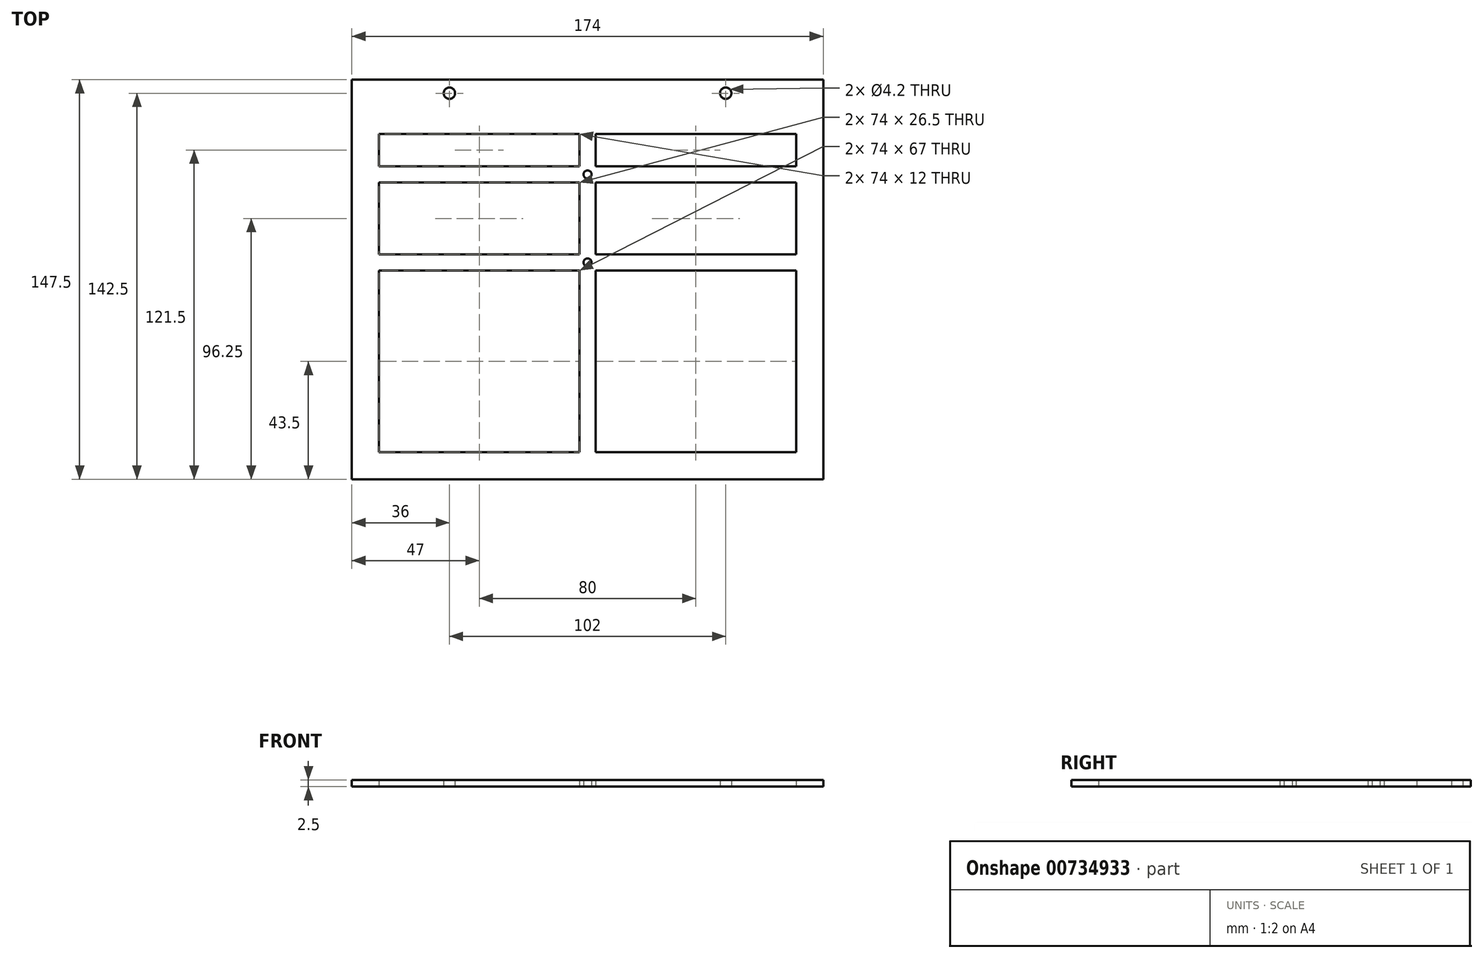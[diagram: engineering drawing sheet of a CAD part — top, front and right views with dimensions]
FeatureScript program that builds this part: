
annotation { "Feature Type Name" : "Feature", "Feature Type Description" : "" }
export const myFeature = defineFeature(function(context is Context, id is Id, definition is map)
    precondition{}
    {
        {
            var Q0;
            Q0=qCreatedBy(makeId("Top.planeOp"),FACE);
            var sketch = newSketch(context, id + "F0", { "sketchPlane" : qUnion([Q0])});
            skLineSegment(sketch, "E0.bottom", {"start": v(87, -80) * mm, "end": v(-87, -80) * mm});
            skLineSegment(sketch, "E0.top", {"start": v(87, 67.5) * mm, "end": v(-87, 67.5) * mm});
            skLineSegment(sketch, "E0.left", {"start": v(87, -80) * mm, "end": v(87, 67.5) * mm});
            skLineSegment(sketch, "E0.right", {"start": v(-87, -80) * mm, "end": v(-87, 67.5) * mm});
            skPoint(sketch, "E0.middle", {"position": v(0, 0) * mm});
            skCircle(sketch, "E1", {"center": v(-51, 62.5) * mm, "radius": 2.1 * mm});
            skCircle(sketch, "E2", {"center": v(51, 62.5) * mm, "radius": 2.1 * mm});
            skLineSegment(sketch, "E3.bottom", {"start": v(15, -23.5) * mm, "end": v(-15, -23.5) * mm, "construction": true});
            skLineSegment(sketch, "E3.top", {"start": v(15, 46.5) * mm, "end": v(-15, 46.5) * mm, "construction": true});
            skLineSegment(sketch, "E3.left", {"start": v(15, -23.5) * mm, "end": v(15, 46.5) * mm, "construction": true});
            skLineSegment(sketch, "E3.right", {"start": v(-15, -23.5) * mm, "end": v(-15, 46.5) * mm, "construction": true});
            skPoint(sketch, "E4", {"position": v(0, 46.5) * mm});
            skPoint(sketch, "E5", {"position": v(0, -23.5) * mm});
            skCircle(sketch, "E6", {"center": v(0, 32.5) * mm, "radius": 1.5 * mm});
            skCircle(sketch, "E7", {"center": v(0, 0) * mm, "radius": 1.5 * mm});
            skLineSegment(sketch, "E8", {"start": v(-87, 62.5) * mm, "end": v(87, 62.5) * mm, "construction": true});
            skLineSegment(sketch, "E9", {"start": v(-87, 57.5) * mm, "end": v(87, 57.5) * mm, "construction": true});
            skLineSegment(sketch, "E10.0", {"start": v(87, -70) * mm, "end": v(-87, -70) * mm, "construction": true});
            skLineSegment(sketch, "E11.0", {"start": v(-77, -80) * mm, "end": v(-77, 80) * mm, "construction": true});
            skLineSegment(sketch, "E12.0", {"start": v(77, -75) * mm, "end": v(77, 85) * mm, "construction": true});
            skLineSegment(sketch, "E13.0", {"start": v(-87, 47.5) * mm, "end": v(87, 47.5) * mm, "construction": true});
            skLineSegment(sketch, "E14.bottom", {"start": v(77, -70) * mm, "end": v(3, -70) * mm});
            skLineSegment(sketch, "E14.top", {"start": v(77, 47.5) * mm, "end": v(3, 47.5) * mm});
            skLineSegment(sketch, "E14.left", {"start": v(77, -70) * mm, "end": v(77, 47.5) * mm});
            skLineSegment(sketch, "E14.right", {"start": v(3, -70) * mm, "end": v(3, 47.5) * mm});
            skLineSegment(sketch, "E15.bottom", {"start": v(-77, -70) * mm, "end": v(-3, -70) * mm});
            skLineSegment(sketch, "E15.top", {"start": v(-77, 47.5) * mm, "end": v(-3, 47.5) * mm});
            skLineSegment(sketch, "E15.left", {"start": v(-77, -70) * mm, "end": v(-77, 47.5) * mm});
            skLineSegment(sketch, "E15.right", {"start": v(-3, -70) * mm, "end": v(-3, 47.5) * mm});
            skLineSegment(sketch, "E16.bottom", {"start": v(-77, 35.5) * mm, "end": v(77, 35.5) * mm});
            skLineSegment(sketch, "E16.top", {"start": v(-77, 29.5) * mm, "end": v(77, 29.5) * mm});
            skLineSegment(sketch, "E16.left", {"start": v(-77, 35.5) * mm, "end": v(-77, 29.5) * mm});
            skLineSegment(sketch, "E16.right", {"start": v(77, 35.5) * mm, "end": v(77, 29.5) * mm});
            skLineSegment(sketch, "E17.bottom", {"start": v(-77, 3) * mm, "end": v(77, 3) * mm});
            skLineSegment(sketch, "E17.top", {"start": v(-77, -3) * mm, "end": v(77, -3) * mm});
            skLineSegment(sketch, "E17.left", {"start": v(-77, 3) * mm, "end": v(-77, -3) * mm});
            skLineSegment(sketch, "E17.right", {"start": v(77, 3) * mm, "end": v(77, -3) * mm});
            skPoint(sketch, "E18", {"position": v(30.07, 0) * mm});
            skSolve(sketch);
        }
        {
            var Q0;
            Q0=makeQuery(id+"F0.imprint","IMPRINT",FACE,{"disambiguationData":[TD([[makeQuery(id+"F0.imprint","IMPRINT",EDGE,{"derivedFrom":sQuery(id+"F0.wireOp",EDGE,"E0.bottom")}),-1.0]])]});
            var Q1;
            Q1=makeQuery(id+"F0.imprint","IMPRINT",FACE,{"disambiguationData":[TD([[makeQuery(id+"F0.imprint","IMPRINT",EDGE,{"derivedFrom":sQuery(id+"F0.wireOp",EDGE,"E6")}),-1.0]])]});
            var Q2;
            {var subQ0=sQuery(id+"F0.wireOp",EDGE,"E16.top");var subQ1=sQuery(id+"F0.wireOp",EDGE,"E14.right");var subQ2=makeQuery(id+"F0.imprint","INTERSECT",VERTEX,{"derivedFrom":[subQ1,subQ0]});Q2=makeQuery(id+"F0.imprint","IMPRINT",FACE,{"disambiguationData":[TD([[makeQuery(id+"F0.imprint","IMPRINT",EDGE,{"disambiguationData":[TD([[subQ2,1.0]])],"derivedFrom":subQ1}),1.0]])]});}
            var Q3;
            Q3=makeQuery(id+"F0.imprint","IMPRINT",FACE,{"disambiguationData":[TD([[makeQuery(id+"F0.imprint","IMPRINT",EDGE,{"derivedFrom":sQuery(id+"F0.wireOp",EDGE,"E7")}),-1.0]])]});
            var Q4;
            {var subQ0=sQuery(id+"F0.wireOp",EDGE,"E17.top");var subQ1=sQuery(id+"F0.wireOp",EDGE,"E14.left");var subQ2=makeQuery(id+"F0.imprint","INTERSECT",VERTEX,{"derivedFrom":[subQ1,subQ0]});Q4=makeQuery(id+"F0.imprint","IMPRINT",FACE,{"disambiguationData":[TD([[makeQuery(id+"F0.imprint","IMPRINT",EDGE,{"disambiguationData":[TD([[subQ2,-1.0]])],"derivedFrom":subQ1}),1.0]])]});}
            var Q5;
            {var subQ0=sQuery(id+"F0.wireOp",EDGE,"E17.top");var subQ1=sQuery(id+"F0.wireOp",EDGE,"E15.left");var subQ2=makeQuery(id+"F0.imprint","INTERSECT",VERTEX,{"derivedFrom":[subQ1,subQ0]});Q5=makeQuery(id+"F0.imprint","IMPRINT",FACE,{"disambiguationData":[TD([[makeQuery(id+"F0.imprint","IMPRINT",EDGE,{"disambiguationData":[TD([[subQ2,-1.0]])],"derivedFrom":subQ1}),-1.0]])]});}
            var Q6;
            {var subQ0=sQuery(id+"F0.wireOp",EDGE,"E16.bottom");var subQ1=sQuery(id+"F0.wireOp",EDGE,"E15.left");var subQ2=makeQuery(id+"F0.imprint","INTERSECT",VERTEX,{"derivedFrom":[subQ1,subQ0]});Q6=makeQuery(id+"F0.imprint","IMPRINT",FACE,{"disambiguationData":[TD([[makeQuery(id+"F0.imprint","IMPRINT",EDGE,{"disambiguationData":[TD([[subQ2,1.0]])],"derivedFrom":subQ1}),-1.0]])]});}
            var Q7;
            {var subQ0=sQuery(id+"F0.wireOp",EDGE,"E16.bottom");var subQ1=sQuery(id+"F0.wireOp",EDGE,"E14.left");var subQ2=makeQuery(id+"F0.imprint","INTERSECT",VERTEX,{"derivedFrom":[subQ1,subQ0]});Q7=makeQuery(id+"F0.imprint","IMPRINT",FACE,{"disambiguationData":[TD([[makeQuery(id+"F0.imprint","IMPRINT",EDGE,{"disambiguationData":[TD([[subQ2,1.0]])],"derivedFrom":subQ1}),1.0]])]});}
            extrude(context, id + "F1", {"entities" : qUnion([Q0, Q1, Q2, Q3, Q4, Q5, Q6, Q7]), "depth" : 2.5 * mm, "offsetDistance" : 25 * mm});
        }
    });
